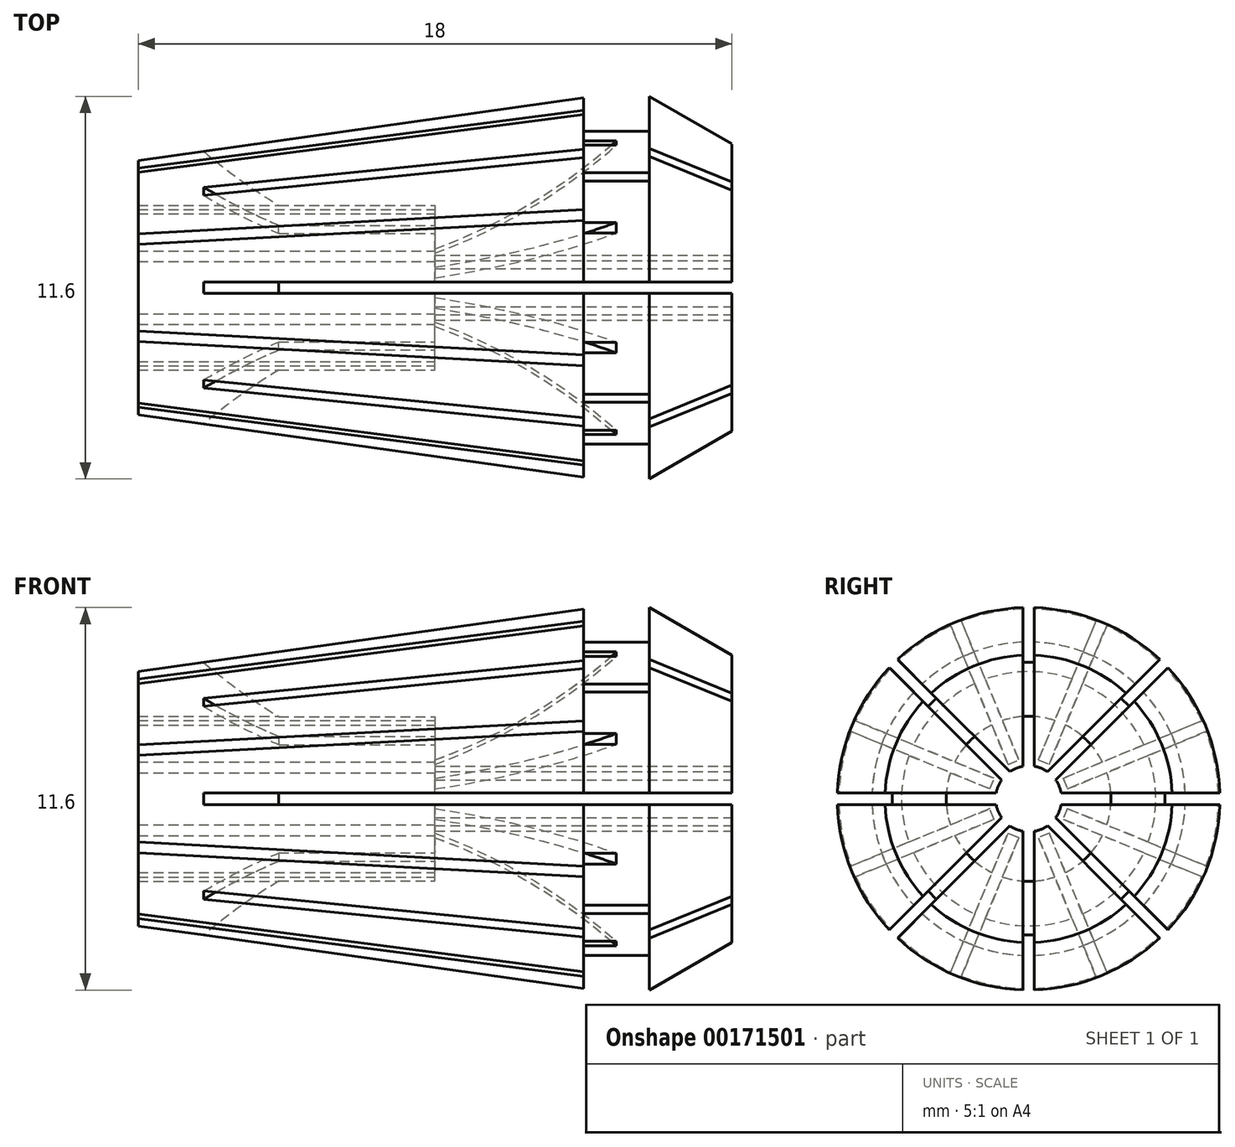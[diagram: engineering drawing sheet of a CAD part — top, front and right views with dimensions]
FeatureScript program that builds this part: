
annotation { "Feature Type Name" : "Feature", "Feature Type Description" : "" }
export const myFeature = defineFeature(function(context is Context, id is Id, definition is map)
    precondition{}
    {
        {
            assignVariable(context, id + "F0", {"name" : "s", "anyValue" : .35 * mm});
        }
        {
            var Q0;
            Q0=qCreatedBy(makeId("Front.planeOp"),FACE);
            var sketch = newSketch(context, id + "F1", { "sketchPlane" : qUnion([Q0])});
            skLineSegment(sketch, "E0", {"start": v(0, 0) * mm, "end": v(-18.8, 0) * mm, "construction": true});
            skLineSegment(sketch, "E1", {"start": v(0, 1) * mm, "end": v(-9, 1) * mm});
            skLineSegment(sketch, "E2", {"start": v(-9, 1) * mm, "end": v(-9, 2.5) * mm});
            skLineSegment(sketch, "E3", {"start": v(-9, 2.5) * mm, "end": v(-18, 2.5) * mm});
            skLineSegment(sketch, "E4", {"start": v(-18, 2.5) * mm, "end": v(-18, 3.86) * mm});
            skLineSegment(sketch, "E5", {"start": v(-18, 3.86) * mm, "end": v(-4.5, 5.75) * mm});
            skLineSegment(sketch, "E6", {"start": v(-4.5, 5.75) * mm, "end": v(-4.5, 4.75) * mm});
            skLineSegment(sketch, "E7", {"start": v(-4.5, 4.75) * mm, "end": v(-2.5, 4.75) * mm});
            skLineSegment(sketch, "E8", {"start": v(-2.5, 4.75) * mm, "end": v(-2.5, 5.8) * mm});
            skLineSegment(sketch, "E9", {"start": v(-2.5, 5.8) * mm, "end": v(0, 4.36) * mm});
            skLineSegment(sketch, "E10", {"start": v(0, 4.36) * mm, "end": v(0, 1) * mm});
            skPoint(sketch, "E11", {"position": v(-6.3, 5.5) * mm});
            skSolve(sketch);
        }
        {
            var Q0;
            Q0=makeQuery(id+"F1.imprint","IMPRINT",FACE,{"disambiguationData":[TD([[makeQuery(id+"F1.imprint","IMPRINT",EDGE,{"derivedFrom":sQuery(id+"F1.wireOp",EDGE,"E1")}),-1.0]])]});
            var Q1;
            Q1=sQuery(id+"F1.wireOp",EDGE,"E0");
            revolve(context, id + "F2", {"entities" : qUnion([Q0]), "axis" : qUnion([Q1]), "revolveType" : RevolveType.FULL});
        }
        {
            var Q0;
            Q0=qCreatedBy(makeId("Front.planeOp"),FACE);
            var sketch = newSketch(context, id + "F3", { "sketchPlane" : qUnion([Q0])});
            skArc(sketch, "E12", {"start": v(-16.02, 4.13) * mm, "mid": v(-12.71, 1.92) * mm, "end": v(-9, 0.5) * mm});
            skLineSegment(sketch, "E13", {"start": v(0, 0) * mm, "end": v(0, 0.5) * mm, "construction": true});
            skLineSegment(sketch, "E14", {"start": v(0, 0.5) * mm, "end": v(0, 1) * mm, "construction": true});
            skLineSegment(sketch, "E15", {"start": v(-9, 0) * mm, "end": v(-9, 0.5) * mm, "construction": true});
            skLineSegment(sketch, "E16", {"start": v(-9, 0.5) * mm, "end": v(-9, 1) * mm, "construction": true});
            skLineSegment(sketch, "E17", {"start": v(0, 0.5) * mm, "end": v(0, 4.36) * mm});
            skLineSegment(sketch, "E18", {"start": v(0, 4.36) * mm, "end": v(-2.5, 5.8) * mm});
            skLineSegment(sketch, "E19", {"start": v(-2.5, 5.8) * mm, "end": v(-4.5, 5.75) * mm});
            skLineSegment(sketch, "E20", {"start": v(-4.5, 5.75) * mm, "end": v(-16.02, 4.13) * mm});
            skLineSegment(sketch, "E21", {"start": v(-9, 0.5) * mm, "end": v(0, 0.5) * mm});
            skSolve(sketch);
        }
        {
            var Q0;
            Q0=makeQuery(id+"F3.imprint","IMPRINT",FACE,{"disambiguationData":[TD([[makeQuery(id+"F3.imprint","IMPRINT",EDGE,{"derivedFrom":sQuery(id+"F3.wireOp",EDGE,"E12")}),1.0]])]});
            extrude(context, id + "F4", {"entities" : qUnion([Q0]), "oppositeDirection" : true, "depth" : getVariable(context, 's') / 2, "hasSecondDirection" : true, "secondDirectionOppositeDirection" : false, "secondDirectionDepth" : getVariable(context, 's') / 2});
        }
        {
            var Q0;
            Q0=makeQuery(id+"F4.opExtrude","SWEPT_BODY",BODY,{"disambiguationData":[OSD([sQuery(id+"F3.wireOp",EDGE,"E12"),sQuery(id+"F3.wireOp",EDGE,"E17"),sQuery(id+"F3.wireOp",EDGE,"E18"),sQuery(id+"F3.wireOp",EDGE,"E19"),sQuery(id+"F3.wireOp",EDGE,"E20"),sQuery(id+"F3.wireOp",EDGE,"E21")])]});
            var Q1;
            Q1=sQuery(id+"F1.wireOp",EDGE,"E0");
            circularPattern(context, id + "F5", {"operationType" : NewBodyOperationType.REMOVE, "entities" : qUnion([Q0]), "axis" : qUnion([Q1]), "angle" : 360 * degree, "instanceCount" : 8, "equalSpace" : true, "computeTransformsWithoutBuiltin" : true});
        }
        {
            var Q0;
            Q0=qCreatedBy(makeId("Front.planeOp"),FACE);
            var sketch = newSketch(context, id + "F6", { "sketchPlane" : qUnion([Q0])});
            skArc(sketch, "E22", {"start": v(-9, 1.2) * mm, "mid": v(-6.08, 2.7) * mm, "end": v(-3.5, 4.75) * mm});
            skLineSegment(sketch, "E23", {"start": v(-18, 3.86) * mm, "end": v(-4.5, 5.75) * mm});
            skLineSegment(sketch, "E24", {"start": v(-4.5, 5.75) * mm, "end": v(-4.5, 4.75) * mm});
            skLineSegment(sketch, "E25", {"start": v(-4.5, 4.75) * mm, "end": v(-3.5, 4.75) * mm});
            skLineSegment(sketch, "E26", {"start": v(-18, 2) * mm, "end": v(-9, 2) * mm});
            skLineSegment(sketch, "E27", {"start": v(-9, 2) * mm, "end": v(-9, 1.2) * mm});
            skLineSegment(sketch, "E28", {"start": v(-18, 3.86) * mm, "end": v(-18, 2) * mm});
            skSolve(sketch);
        }
        {
            var Q0;
            Q0 = qSketchRegion(id + "F6", true);
            extrude(context, id + "F7", {"entities" : qUnion([Q0]), "depth" : getVariable(context, 's') / 2, "hasSecondDirection" : true, "secondDirectionOppositeDirection" : true, "secondDirectionDepth" : getVariable(context, 's') / 2});
        }
        {
            var Q0;
            Q0=makeQuery(id+"F7.opExtrude","SWEPT_BODY",BODY,{"disambiguationData":[OSD([sQuery(id+"F6.wireOp",EDGE,"E22"),sQuery(id+"F6.wireOp",EDGE,"E23"),sQuery(id+"F6.wireOp",EDGE,"E24"),sQuery(id+"F6.wireOp",EDGE,"E25"),sQuery(id+"F6.wireOp",EDGE,"CWTkhczA-MISY-V16c-OO6U-PYNv21l9aHGo"),sQuery(id+"F6.wireOp",EDGE,"E26"),sQuery(id+"F6.wireOp",EDGE,"E27")])]});
            var Q1;
            Q1=sQuery(id+"F1.wireOp",EDGE,"E0");
            transform(context, id + "F8", {"entities" : qUnion([Q0]), "transformType" : TransformType.ROTATION, "transformAxis" : qUnion([Q1]), "angle" : 22.5 * degree, "makeCopy" : false});
        }
        {
            var Q0;
            Q0=makeQuery(id+"F7.opExtrude","SWEPT_BODY",BODY,{"disambiguationData":[OSD([sQuery(id+"F6.wireOp",EDGE,"E22"),sQuery(id+"F6.wireOp",EDGE,"E23"),sQuery(id+"F6.wireOp",EDGE,"E24"),sQuery(id+"F6.wireOp",EDGE,"E25"),sQuery(id+"F6.wireOp",EDGE,"CWTkhczA-MISY-V16c-OO6U-PYNv21l9aHGo"),sQuery(id+"F6.wireOp",EDGE,"E26"),sQuery(id+"F6.wireOp",EDGE,"E27")])]});
            var Q1;
            Q1=sQuery(id+"F1.wireOp",EDGE,"E0");
            circularPattern(context, id + "F9", {"operationType" : NewBodyOperationType.REMOVE, "entities" : qUnion([Q0]), "axis" : qUnion([Q1]), "angle" : 360 * degree, "instanceCount" : 8, "equalSpace" : true, "computeTransformsWithoutBuiltin" : true});
        }
    });
